# Revit family: KINGSLEY Shower Head Round
name_source: partatom
category: Generic Models
units: mm (PartAtom-declared; Revit-internal decimal feet)

## family parameters
Always vertical = Yes
Can host rebar = No
Cut with Voids When Loaded = No
Maintain Annotation Orientation = No
OmniClass Number = 23.31.17.19
Part Type = Normal
Room Calculation Point = No
Round Connector Dimension = Use Diameter
Shared = No
Work Plane-Based = No

## types (1)
- KINGSLEY Shower Head Round
    Default Elevation = 0 mm  [stored 0 ft]
    Description = KINGSLEY Shower Head Round
    Manufacturer = ABI Interiors PTY LTD
    Model = Brass (12657), Nickel (13996) Chrome AU/NZ (12658)
    URL = https://www.abiinteriors.com.au
    URL - NZ = https://www.abiinteriors.co.nz
    URL - UK = https://www.abiinteriors.co.uk
    URL _ AUS = https://www.abiinteriors.com.au

note: [stored X ft] marks values corroborated as IEEE doubles in the binary element streams (Revit-internal decimal feet)

## geometry (parser evidence)
native form markers: Sweep x2
no freeform markers — native parametric forms only
